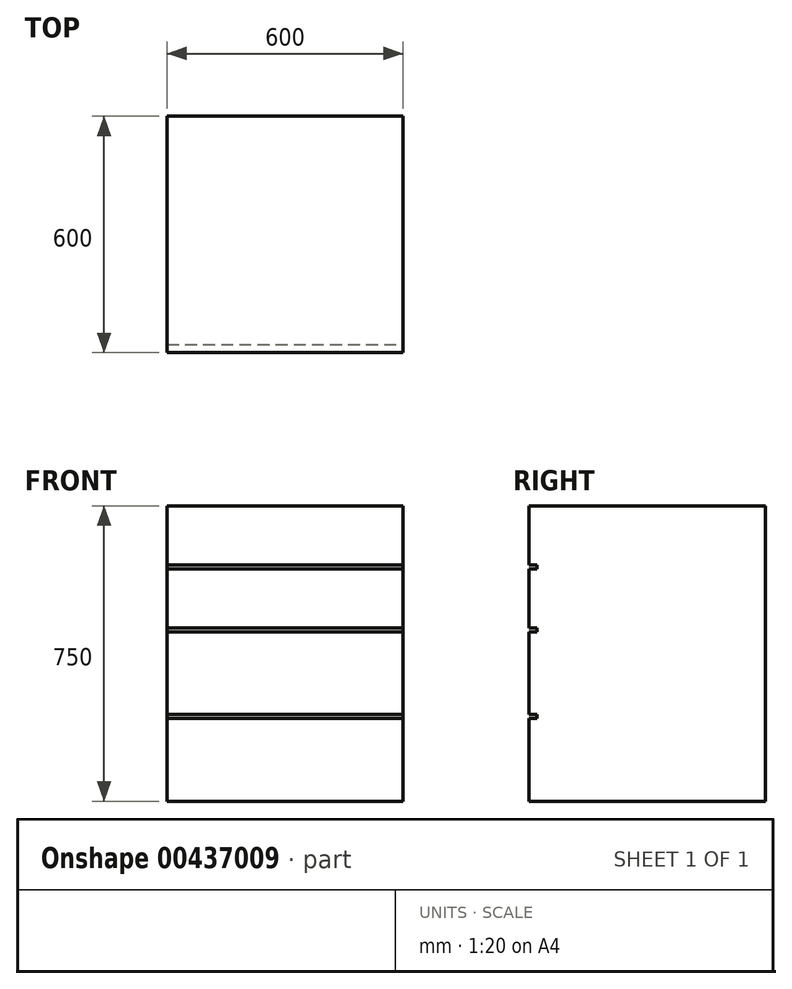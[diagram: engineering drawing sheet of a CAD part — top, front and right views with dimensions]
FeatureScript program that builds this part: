
annotation { "Feature Type Name" : "Feature", "Feature Type Description" : "" }
export const myFeature = defineFeature(function(context is Context, id is Id, definition is map)
    precondition{}
    {
        {
            var Q0;
            Q0=qCreatedBy(makeId("Right.planeOp"),FACE);
            var sketch = newSketch(context, id + "F0", { "sketchPlane" : qUnion([Q0])});
            skLineSegment(sketch, "E0.top", {"start": v(0, 750) * mm, "end": v(-600, 750) * mm});
            skLineSegment(sketch, "E0.left", {"start": v(0, 0) * mm, "end": v(0, 750) * mm});
            skLineSegment(sketch, "E0.right", {"start": v(-600, 0) * mm, "end": v(-600, 750) * mm});
            skLineSegment(sketch, "E1", {"start": v(0, 0) * mm, "end": v(-600, 0) * mm});
            skSolve(sketch);
        }
        {
            var Q0;
            Q0=qSketchRegion(id+"F0",true);
            extrude(context, id + "F1", {"entities" : qUnion([Q0]), "depth" : 600 * mm});
        }
        {
            var Q0;
            Q0=makeQuery(id+"F1.opExtrude","SWEPT_FACE",FACE,{"disambiguationData":[OSD([sQuery(id+"F0.wireOp",EDGE,"E0.right")])]});
            var sketch = newSketch(context, id + "F2", { "sketchPlane" : qUnion([Q0])});
            skLineSegment(sketch, "E2.bottom", {"start": v(0, 600) * mm, "end": v(600, 600) * mm});
            skLineSegment(sketch, "E2.top", {"start": v(0, 590) * mm, "end": v(600, 590) * mm});
            skLineSegment(sketch, "E2.left", {"start": v(0, 600) * mm, "end": v(0, 590) * mm});
            skLineSegment(sketch, "E2.right", {"start": v(600, 600) * mm, "end": v(600, 590) * mm});
            skLineSegment(sketch, "E3.bottom", {"start": v(0, 440) * mm, "end": v(600, 440) * mm});
            skLineSegment(sketch, "E3.top", {"start": v(0, 430) * mm, "end": v(600, 430) * mm});
            skLineSegment(sketch, "E3.left", {"start": v(0, 440) * mm, "end": v(0, 430) * mm});
            skLineSegment(sketch, "E3.right", {"start": v(600, 440) * mm, "end": v(600, 430) * mm});
            skLineSegment(sketch, "E4.bottom", {"start": v(0, 220) * mm, "end": v(600, 220) * mm});
            skLineSegment(sketch, "E4.top", {"start": v(0, 210) * mm, "end": v(600, 210) * mm});
            skLineSegment(sketch, "E4.left", {"start": v(0, 220) * mm, "end": v(0, 210) * mm});
            skLineSegment(sketch, "E4.right", {"start": v(600, 220) * mm, "end": v(600, 210) * mm});
            skSolve(sketch);
        }
        {
            var Q0;
            Q0=qSketchRegion(id+"F2",true);
            extrude(context, id + "F3", {"entities" : qUnion([Q0]), "operationType" : NewBodyOperationType.REMOVE, "oppositeDirection" : true, "depth" : 20 * mm});
        }
    });
